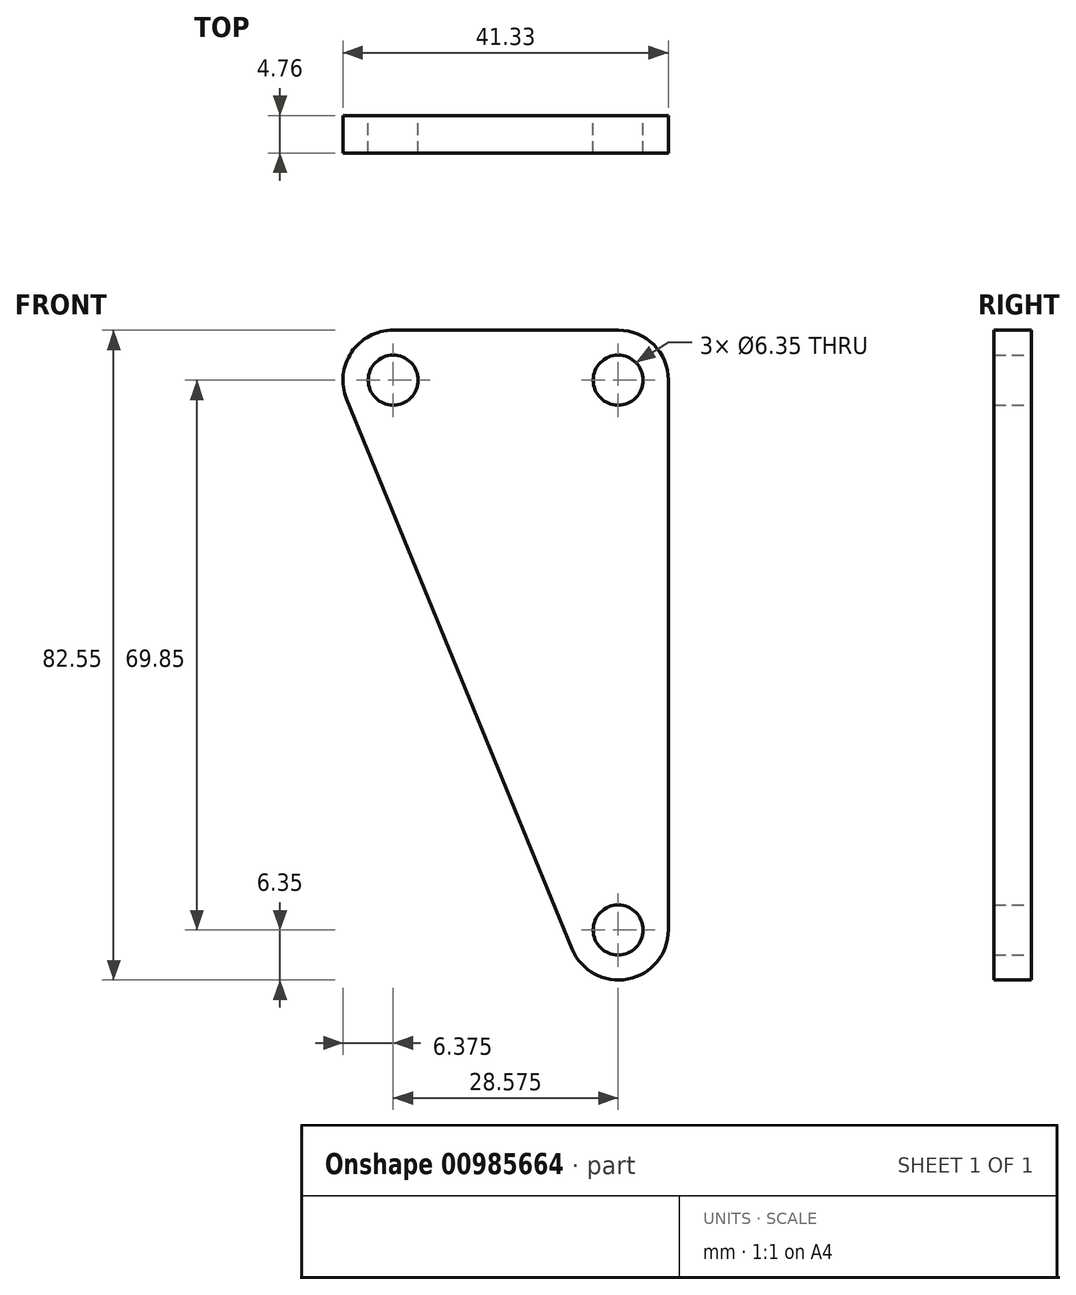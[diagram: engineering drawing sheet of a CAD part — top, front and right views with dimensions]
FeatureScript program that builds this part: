
annotation { "Feature Type Name" : "Feature", "Feature Type Description" : "" }
export const myFeature = defineFeature(function(context is Context, id is Id, definition is map)
    precondition{}
    {
        {
            var Q0;
            Q0=qCreatedBy(makeId("Front.planeOp"),FACE);
            var sketch = newSketch(context, id + "F0", { "sketchPlane" : qUnion([Q0])});
            skLineSegment(sketch, "E0", {"start": v(0, -38.1) * mm, "end": v(0, 31.75) * mm});
            skLineSegment(sketch, "E1", {"start": v(-6.35, 38.1) * mm, "end": v(-34.98, 38.1) * mm});
            skLineSegment(sketch, "E2", {"start": v(-40.86, 29.34) * mm, "end": v(-12.23, -40.5) * mm});
            skPoint(sketch, "E3.visualSharp", {"position": v(-44.45, 38.1) * mm});
            skArc(sketch, "E3.filletArc", {"start": v(-34.98, 38.1) * mm, "mid": v(-40.26, 35.29) * mm, "end": v(-40.86, 29.34) * mm});
            skPoint(sketch, "E4.visualSharp", {"position": v(0, -70.33) * mm});
            skArc(sketch, "E4.filletArc", {"start": v(-12.23, -40.5) * mm, "mid": v(-5.12, -44.33) * mm, "end": v(0, -38.1) * mm});
            skCircle(sketch, "E5", {"center": v(-6.38, 31.75) * mm, "radius": 3.18 * mm});
            skCircle(sketch, "E6", {"center": v(-34.95, 31.75) * mm, "radius": 3.18 * mm});
            skCircle(sketch, "E7", {"center": v(-6.38, -38.1) * mm, "radius": 3.18 * mm});
            skPoint(sketch, "E8.visualSharp", {"position": v(0, 38.1) * mm});
            skArc(sketch, "E8.filletArc", {"start": v(0, 31.75) * mm, "mid": v(-1.86, 36.24) * mm, "end": v(-6.35, 38.1) * mm});
            skLineSegment(sketch, "E9", {"start": v(-20.67, 38.1) * mm, "end": v(-20.67, 30.45) * mm});
            skSolve(sketch);
        }
        {
            var Q0;
            Q0 = qSketchRegion(id + "F0", true);
            extrude(context, id + "F1", {"entities" : qUnion([Q0]), "depth" : 4.76 * mm, "offsetDistance" : 25.4 * mm});
        }
    });
